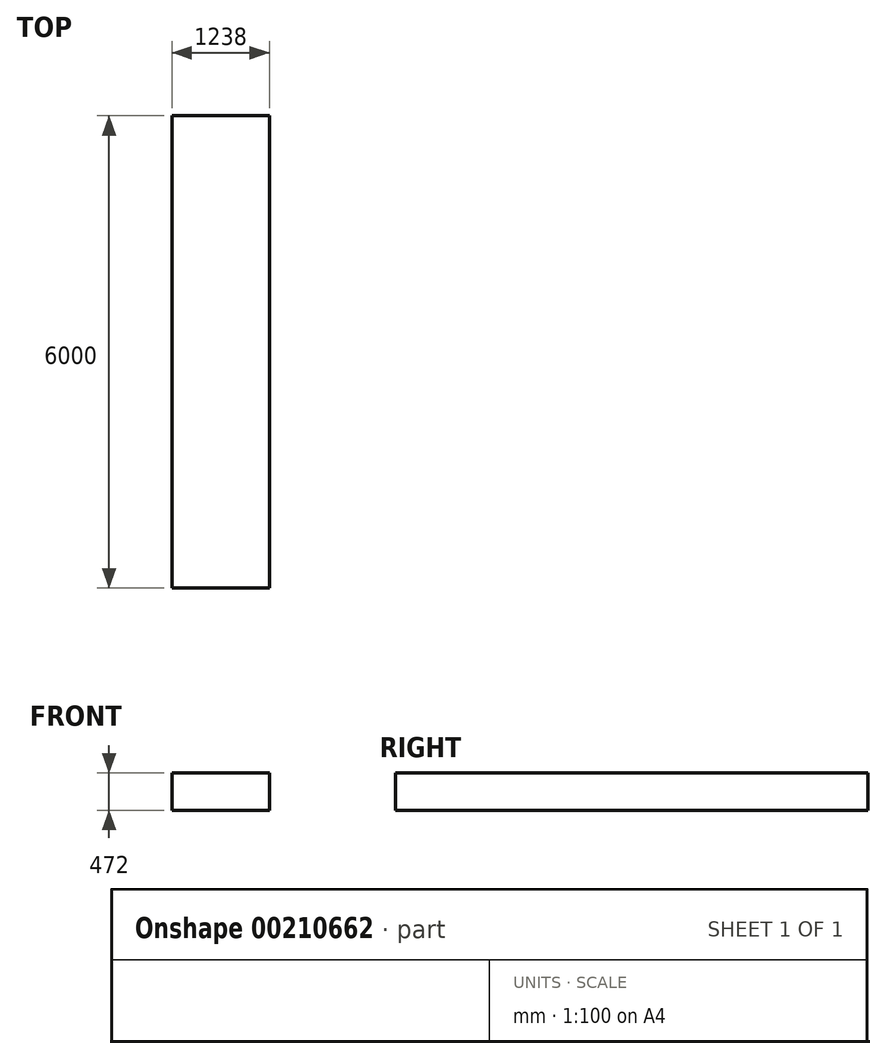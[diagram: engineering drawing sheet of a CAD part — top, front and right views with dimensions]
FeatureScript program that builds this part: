
annotation { "Feature Type Name" : "Feature", "Feature Type Description" : "" }
export const myFeature = defineFeature(function(context is Context, id is Id, definition is map)
    precondition{}
    {
        {
            var Q0;
            Q0=qCreatedBy(makeId("Top.planeOp"),FACE);
            var sketch = newSketch(context, id + "F0", { "sketchPlane" : qUnion([Q0])});
            skLineSegment(sketch, "E0.bottom", {"start": v(0, 0) * mm, "end": v(5978, 0) * mm});
            skLineSegment(sketch, "E0.top", {"start": v(0, 20013) * mm, "end": v(5978, 20013) * mm});
            skLineSegment(sketch, "E0.left", {"start": v(0, 0) * mm, "end": v(0, 20013) * mm});
            skLineSegment(sketch, "E0.right", {"start": v(5978, 0) * mm, "end": v(5978, 20013) * mm});
            skLineSegment(sketch, "E1.bottom", {"start": v(0, 0) * mm, "end": v(1238, 0) * mm});
            skLineSegment(sketch, "E1.top", {"start": v(0, 6000) * mm, "end": v(1238, 6000) * mm});
            skLineSegment(sketch, "E1.left", {"start": v(0, 0) * mm, "end": v(0, 6000) * mm});
            skLineSegment(sketch, "E1.right", {"start": v(1238, 0) * mm, "end": v(1238, 6000) * mm});
            skLineSegment(sketch, "E2.bottom", {"start": v(0, 7998) * mm, "end": v(1000, 7998) * mm});
            skLineSegment(sketch, "E2.top", {"start": v(0, 12048) * mm, "end": v(1000, 12048) * mm});
            skLineSegment(sketch, "E2.left", {"start": v(0, 7998) * mm, "end": v(0, 12048) * mm});
            skLineSegment(sketch, "E2.right", {"start": v(1000, 7998) * mm, "end": v(1000, 12048) * mm});
            skSolve(sketch);
        }
        {
            var Q0;
            Q0=makeQuery(id+"F0.imprint","IMPRINT",FACE,{"disambiguationData":[TD([[makeQuery(id+"F0.imprint","IMPRINT",EDGE,{"derivedFrom":sQuery(id+"F0.wireOp",EDGE,"E0.bottom")}),1.0]])]});
            extrude(context, id + "F1", {"entities" : qUnion([Q0]), "depth" : (450 + 22) * mm});
        }
    });
